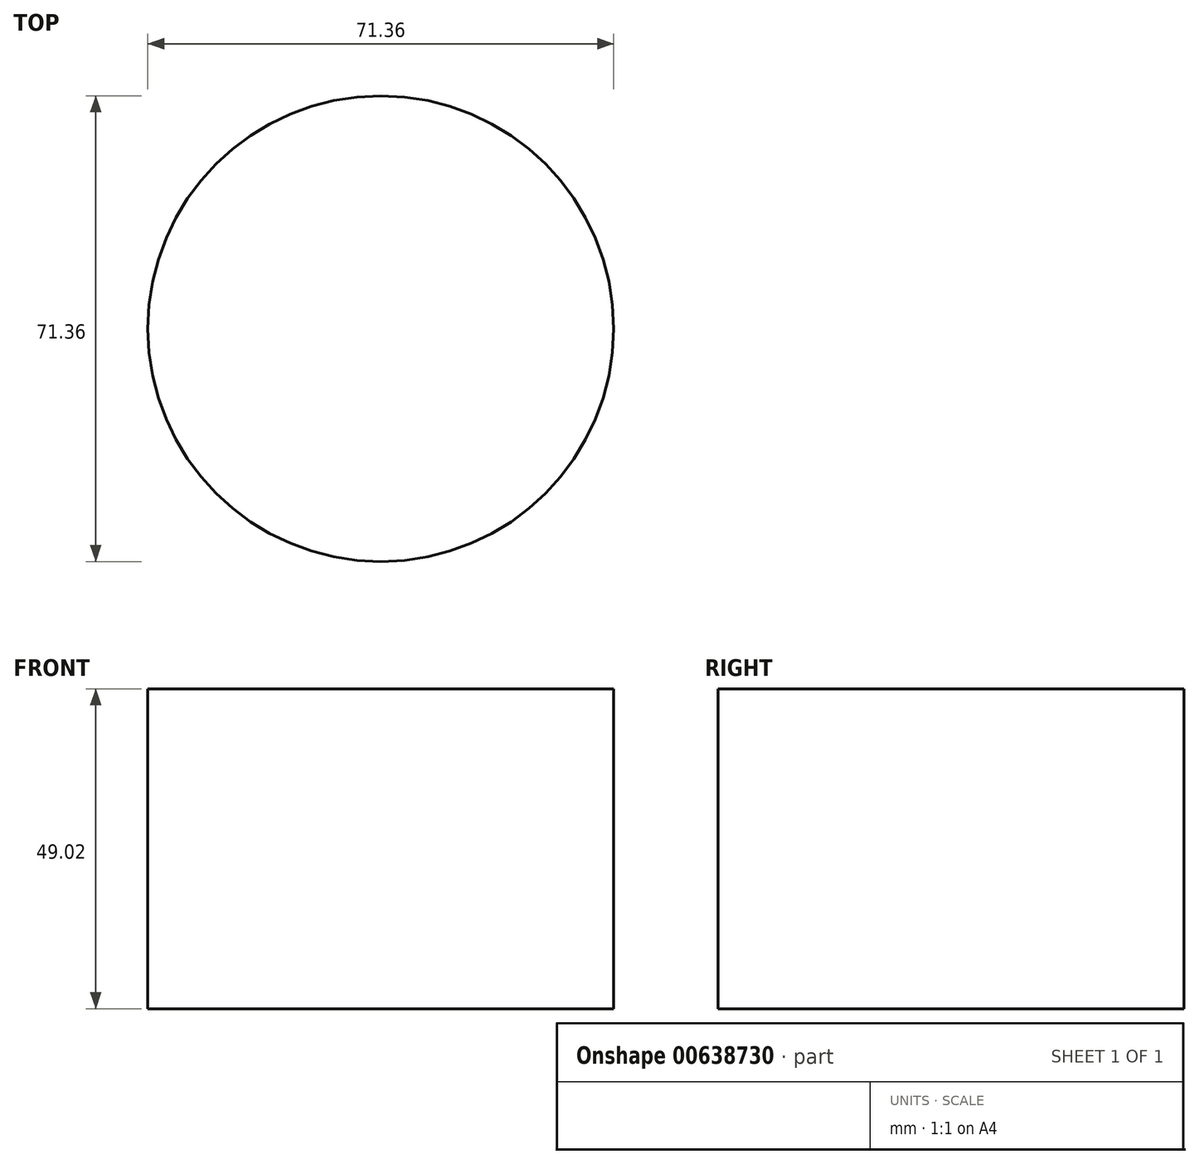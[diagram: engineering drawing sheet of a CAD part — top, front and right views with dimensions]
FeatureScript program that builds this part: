
annotation { "Feature Type Name" : "Feature", "Feature Type Description" : "" }
export const myFeature = defineFeature(function(context is Context, id is Id, definition is map)
    precondition{}
    {
        {
            var Q0;
            Q0=qCreatedBy(makeId("Top.planeOp"),FACE);
            var sketch = newSketch(context, id + "F0", { "sketchPlane" : qUnion([Q0])});
            skCircle(sketch, "E0", {"center": v(0, 0) * mm, "radius": 35.68 * mm});
            skSolve(sketch);
        }
        {
            var Q0;
            Q0=makeQuery(id+"F0.imprint","IMPRINT",FACE,{"disambiguationData":[TD([[makeQuery(id+"F0.imprint","IMPRINT",EDGE,{"derivedFrom":sQuery(id+"F0.wireOp",EDGE,"E0")}),1.0]])]});
            extrude(context, id + "F1", {"entities" : qUnion([Q0]), "depth" : 49.02 * mm, "offsetDistance" : 25.4 * mm});
        }
    });
